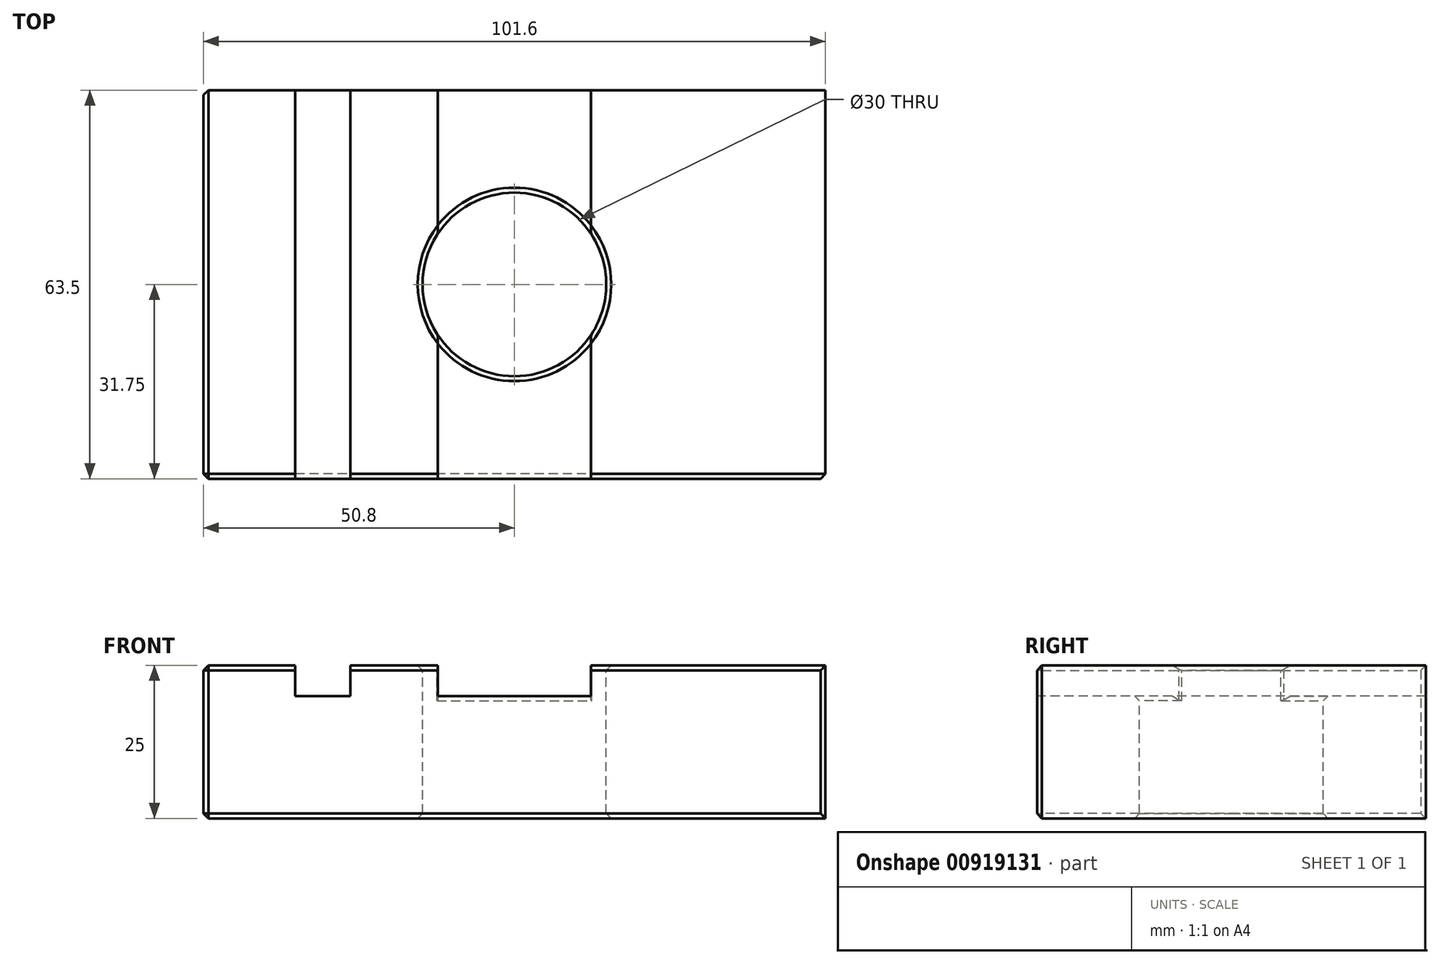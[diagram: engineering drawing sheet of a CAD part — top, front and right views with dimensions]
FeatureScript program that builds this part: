
annotation { "Feature Type Name" : "Feature", "Feature Type Description" : "" }
export const myFeature = defineFeature(function(context is Context, id is Id, definition is map)
    precondition{}
    {
        {
            var Q0;
            Q0=qCreatedBy(makeId("Top.planeOp"),FACE);
            var sketch = newSketch(context, id + "F0", { "sketchPlane" : qUnion([Q0])});
            skLineSegment(sketch, "E0.bottom", {"start": v(-50.8, -31.75) * mm, "end": v(50.8, -31.75) * mm});
            skLineSegment(sketch, "E0.top", {"start": v(-50.8, 31.75) * mm, "end": v(50.8, 31.75) * mm});
            skLineSegment(sketch, "E0.left", {"start": v(-50.8, -31.75) * mm, "end": v(-50.8, 31.75) * mm});
            skLineSegment(sketch, "E0.right", {"start": v(50.8, -31.75) * mm, "end": v(50.8, 31.75) * mm});
            skPoint(sketch, "E0.middle", {"position": v(0, 0) * mm});
            skSolve(sketch);
        }
        {
            var Q0;
            Q0=makeQuery(id+"F0.imprint","IMPRINT",FACE,{"disambiguationData":[TD([[makeQuery(id+"F0.imprint","IMPRINT",EDGE,{"derivedFrom":sQuery(id+"F0.wireOp",EDGE,"E0.bottom")}),1.0]])]});
            extrude(context, id + "F1", {"entities" : qUnion([Q0]), "depth" : 25 * mm, "offsetDistance" : 25.4 * mm});
        }
        {
            var Q0;
            Q0=makeQuery(id+"F1.opExtrude","CAP_FACE",FACE,{"disambiguationData":[OSD([sQuery(id+"F0.wireOp",EDGE,"E0.bottom"),sQuery(id+"F0.wireOp",EDGE,"E0.top"),sQuery(id+"F0.wireOp",EDGE,"E0.left"),sQuery(id+"F0.wireOp",EDGE,"E0.right")])],"isStart":false});
            var sketch = newSketch(context, id + "F2", { "sketchPlane" : qUnion([Q0])});
            skCircle(sketch, "E1", {"center": v(0, 0) * mm, "radius": 15 * mm});
            skSolve(sketch);
        }
        {
            var Q0;
            Q0=makeQuery(id+"F2.imprint","IMPRINT",FACE,{"disambiguationData":[TD([[makeQuery(id+"F2.imprint","IMPRINT",EDGE,{"derivedFrom":sQuery(id+"F2.wireOp",EDGE,"E1")}),1.0]])]});
            extrude(context, id + "F3", {"entities" : qUnion([Q0]), "operationType" : NewBodyOperationType.REMOVE, "endBound" : BoundingType.THROUGH_ALL, "oppositeDirection" : true, "depth" : 25 * mm, "offsetDistance" : 25 * mm});
        }
        {
            var Q0;
            Q0=makeQuery(id+"F1.opExtrude","CAP_FACE",FACE,{"disambiguationData":[OSD([sQuery(id+"F0.wireOp",EDGE,"E0.bottom"),sQuery(id+"F0.wireOp",EDGE,"E0.top"),sQuery(id+"F0.wireOp",EDGE,"E0.left"),sQuery(id+"F0.wireOp",EDGE,"E0.right")])],"isStart":false});
            var sketch = newSketch(context, id + "F4", { "sketchPlane" : qUnion([Q0])});
            skLineSegment(sketch, "E2", {"start": v(-35.8, 31.75) * mm, "end": v(-35.8, -31.75) * mm});
            skLineSegment(sketch, "E3", {"start": v(-35.8, -31.75) * mm, "end": v(-26.8, -31.75) * mm});
            skLineSegment(sketch, "E4", {"start": v(-26.8, -31.75) * mm, "end": v(-26.8, 31.75) * mm});
            skLineSegment(sketch, "E5", {"start": v(-26.8, 31.75) * mm, "end": v(-35.8, 31.75) * mm});
            skLineSegment(sketch, "E6", {"start": v(-12.5, 31.75) * mm, "end": v(-12.5, -31.75) * mm});
            skLineSegment(sketch, "E7", {"start": v(-12.5, -31.75) * mm, "end": v(12.5, -31.75) * mm});
            skLineSegment(sketch, "E8", {"start": v(12.5, -31.75) * mm, "end": v(12.5, 31.75) * mm});
            skLineSegment(sketch, "E9", {"start": v(12.5, 31.75) * mm, "end": v(-12.5, 31.75) * mm});
            skLineSegment(sketch, "E10", {"start": v(0, 31.75) * mm, "end": v(0, -31.75) * mm, "construction": true});
            skSolve(sketch);
        }
        {
            var Q0;
            {var subQ0=sQuery(id+"F4.wireOp",EDGE,"E9");Q0=makeQuery(id+"F4.imprint","IMPRINT",FACE,{"disambiguationData":[TD([[makeQuery(id+"F4.imprint","IMPRINT",EDGE,{"derivedFrom":subQ0}),-1.0]])]});}
            var Q1;
            Q1=makeQuery(id+"F4.imprint","IMPRINT",FACE,{"disambiguationData":[TD([[makeQuery(id+"F4.imprint","IMPRINT",EDGE,{"derivedFrom":sQuery(id+"F4.wireOp",EDGE,"E2")}),1.0]])]});
            var Q2;
            {var subQ0=sQuery(id+"F4.wireOp",EDGE,"E7");Q2=makeQuery(id+"F4.imprint","IMPRINT",FACE,{"disambiguationData":[TD([[makeQuery(id+"F4.imprint","IMPRINT",EDGE,{"derivedFrom":subQ0}),1.0]])]});}
            extrude(context, id + "F5", {"entities" : qUnion([Q0, Q1, Q2]), "operationType" : NewBodyOperationType.REMOVE, "oppositeDirection" : true, "depth" : 5 * mm, "offsetDistance" : 25 * mm});
        }
        {
            var Q0;
            {var subQ0=sQuery(id+"F2.wireOp",EDGE,"E1");var subQ1=makeQuery(id+"F3.boolean.opBoolean","COPY",EDGE,{"derivedFrom":makeQuery(id+"F3.opExtrude","CAP_EDGE",EDGE,{"disambiguationData":[OSD([subQ0])],"isStart":true})});Q0=makeQuery(id+"F5.boolean.opBoolean","COPY",EDGE,{"derivedFrom":makeQuery(id+"F5.opExtrude","CAP_EDGE",EDGE,{"disambiguationData":[OSD([subQ0]),TDD([makeQuery(id+"F4.imprint","IMPRINT",EDGE,{"disambiguationData":[TD([[makeQuery(id+"F4.imprint","INTERSECT",VERTEX,{"disambiguationData":[OD(1.0)],"derivedFrom":[subQ1,sQuery(id+"F4.wireOp",EDGE,"E6")]}),-1.0]])],"derivedFrom":subQ1})])],"isStart":false})});}
            var Q1;
            {var subQ0=sQuery(id+"F4.wireOp",EDGE,"E6");var subQ1=sQuery(id+"F2.wireOp",EDGE,"E1");Q1=makeQuery(id+"F5.boolean.opBoolean","COPY",EDGE,{"derivedFrom":makeQuery(id+"F5.opExtrude","SWEPT_EDGE",EDGE,{"disambiguationData":[OSD([subQ1,subQ0]),TDD([makeQuery(id+"F4.imprint","INTERSECT",VERTEX,{"disambiguationData":[OD(1.0)],"derivedFrom":[makeQuery(id+"F3.boolean.opBoolean","COPY",EDGE,{"derivedFrom":makeQuery(id+"F3.opExtrude","CAP_EDGE",EDGE,{"disambiguationData":[OSD([subQ1])],"isStart":true})}),subQ0]})])]})});}
            var Q2;
            {var subQ2=sQuery(id+"F2.wireOp",EDGE,"E1");var subQ3=sQuery(id+"F4.wireOp",EDGE,"E6");var subQ4=makeQuery(id+"F3.boolean.opBoolean","COPY",EDGE,{"derivedFrom":makeQuery(id+"F3.opExtrude","CAP_EDGE",EDGE,{"disambiguationData":[OSD([subQ2])],"isStart":true})});Q2=makeQuery(id+"F5.boolean.opBoolean","SPLIT",EDGE,{"disambiguationData":[TD([makeQuery(id+"F5.opExtrude","SWEPT_FACE",FACE,{"disambiguationData":[OSD([subQ3]),TDD([makeQuery(id+"F4.imprint","IMPRINT",EDGE,{"disambiguationData":[TD([[makeQuery(id+"F4.imprint","INTERSECT",VERTEX,{"disambiguationData":[OD(0.0)],"derivedFrom":[subQ4,subQ3]}),1.0]])],"derivedFrom":subQ3})])]})])],"derivedFrom":subQ4});}
            var Q3;
            {var subQ0=sQuery(id+"F4.wireOp",EDGE,"E6");var subQ1=sQuery(id+"F2.wireOp",EDGE,"E1");Q3=makeQuery(id+"F5.boolean.opBoolean","COPY",EDGE,{"derivedFrom":makeQuery(id+"F5.opExtrude","SWEPT_EDGE",EDGE,{"disambiguationData":[OSD([subQ1,subQ0]),TDD([makeQuery(id+"F4.imprint","INTERSECT",VERTEX,{"disambiguationData":[OD(0.0)],"derivedFrom":[makeQuery(id+"F3.boolean.opBoolean","COPY",EDGE,{"derivedFrom":makeQuery(id+"F3.opExtrude","CAP_EDGE",EDGE,{"disambiguationData":[OSD([subQ1])],"isStart":true})}),subQ0]})])]})});}
            var Q4;
            {var subQ0=sQuery(id+"F2.wireOp",EDGE,"E1");var subQ1=makeQuery(id+"F3.boolean.opBoolean","COPY",EDGE,{"derivedFrom":makeQuery(id+"F3.opExtrude","CAP_EDGE",EDGE,{"disambiguationData":[OSD([subQ0])],"isStart":true})});Q4=makeQuery(id+"F5.boolean.opBoolean","COPY",EDGE,{"derivedFrom":makeQuery(id+"F5.opExtrude","CAP_EDGE",EDGE,{"disambiguationData":[OSD([subQ0]),TDD([makeQuery(id+"F4.imprint","IMPRINT",EDGE,{"disambiguationData":[TD([[makeQuery(id+"F4.imprint","INTERSECT",VERTEX,{"disambiguationData":[OD(0.0)],"derivedFrom":[subQ1,sQuery(id+"F4.wireOp",EDGE,"E6")]}),1.0]])],"derivedFrom":subQ1})])],"isStart":false})});}
            var Q5;
            {var subQ2=sQuery(id+"F2.wireOp",EDGE,"E1");var subQ3=sQuery(id+"F4.wireOp",EDGE,"E8");var subQ4=makeQuery(id+"F3.boolean.opBoolean","COPY",EDGE,{"derivedFrom":makeQuery(id+"F3.opExtrude","CAP_EDGE",EDGE,{"disambiguationData":[OSD([subQ2])],"isStart":true})});Q5=makeQuery(id+"F5.boolean.opBoolean","SPLIT",EDGE,{"disambiguationData":[TD([makeQuery(id+"F5.opExtrude","SWEPT_FACE",FACE,{"disambiguationData":[OSD([subQ3]),TDD([makeQuery(id+"F4.imprint","IMPRINT",EDGE,{"disambiguationData":[TD([[makeQuery(id+"F4.imprint","INTERSECT",VERTEX,{"disambiguationData":[OD(0.0)],"derivedFrom":[subQ4,subQ3]}),1.0]])],"derivedFrom":subQ3})])]})])],"derivedFrom":subQ4});}
            var Q6;
            {var subQ0=sQuery(id+"F4.wireOp",EDGE,"E8");var subQ1=sQuery(id+"F2.wireOp",EDGE,"E1");Q6=makeQuery(id+"F5.boolean.opBoolean","COPY",EDGE,{"derivedFrom":makeQuery(id+"F5.opExtrude","SWEPT_EDGE",EDGE,{"disambiguationData":[OSD([subQ1,subQ0]),TDD([makeQuery(id+"F4.imprint","INTERSECT",VERTEX,{"disambiguationData":[OD(0.0)],"derivedFrom":[makeQuery(id+"F3.boolean.opBoolean","COPY",EDGE,{"derivedFrom":makeQuery(id+"F3.opExtrude","CAP_EDGE",EDGE,{"disambiguationData":[OSD([subQ1])],"isStart":true})}),subQ0]})])]})});}
            var Q7;
            {var subQ0=sQuery(id+"F4.wireOp",EDGE,"E8");var subQ1=sQuery(id+"F2.wireOp",EDGE,"E1");Q7=makeQuery(id+"F5.boolean.opBoolean","COPY",EDGE,{"derivedFrom":makeQuery(id+"F5.opExtrude","SWEPT_EDGE",EDGE,{"disambiguationData":[OSD([subQ1,subQ0]),TDD([makeQuery(id+"F4.imprint","INTERSECT",VERTEX,{"disambiguationData":[OD(1.0)],"derivedFrom":[makeQuery(id+"F3.boolean.opBoolean","COPY",EDGE,{"derivedFrom":makeQuery(id+"F3.opExtrude","CAP_EDGE",EDGE,{"disambiguationData":[OSD([subQ1])],"isStart":true})}),subQ0]})])]})});}
            var Q8;
            Q8=makeQuery(id+"F3.boolean.opBoolean","COPY",FACE,{"derivedFrom":makeQuery(id+"F3.opExtrude","SWEPT_FACE",FACE,{"disambiguationData":[OSD([sQuery(id+"F2.wireOp",EDGE,"E1")])]})});
            chamfer(context, id + "F6", {"entities" : qUnion([Q0, Q1, Q2, Q3, Q4, Q5, Q6, Q7, Q8]), "width" : .8 * mm, "tangentPropagation" : true});
        }
        {
            var Q0;
            {var subQ0=sQuery(id+"F0.wireOp",EDGE,"E0.bottom");var subQ2=makeQuery(id+"F1.opExtrude","CAP_EDGE",EDGE,{"disambiguationData":[OSD([subQ0])],"isStart":false});Q0=makeQuery(id+"F5.boolean.opBoolean","SPLIT",EDGE,{"disambiguationData":[TD([makeQuery(id+"F5.opExtrude","SWEPT_FACE",FACE,{"disambiguationData":[OSD([sQuery(id+"F4.wireOp",EDGE,"E4")])]})])],"derivedFrom":subQ2});}
            var Q1;
            {var subQ0=sQuery(id+"F0.wireOp",EDGE,"E0.bottom");var subQ1=sQuery(id+"F0.wireOp",EDGE,"E0.right");var subQ3=makeQuery(id+"F1.opExtrude","CAP_EDGE",EDGE,{"disambiguationData":[OSD([subQ0])],"isStart":false});Q1=makeQuery(id+"F5.boolean.opBoolean","SPLIT",EDGE,{"disambiguationData":[TD([makeQuery(id+"F1.opExtrude","SWEPT_FACE",FACE,{"disambiguationData":[OSD([subQ1])]})])],"derivedFrom":subQ3});}
            var Q2;
            {var subQ0=sQuery(id+"F0.wireOp",EDGE,"E0.bottom");var subQ1=sQuery(id+"F0.wireOp",EDGE,"E0.left");Q2=makeQuery(id+"F5.boolean.opBoolean","SPLIT",EDGE,{"disambiguationData":[TD([makeQuery(id+"F1.opExtrude","SWEPT_FACE",FACE,{"disambiguationData":[OSD([subQ1])]})])],"derivedFrom":makeQuery(id+"F1.opExtrude","CAP_EDGE",EDGE,{"disambiguationData":[OSD([subQ0])],"isStart":false})});}
            var Q3;
            Q3=makeQuery(id+"F5.boolean.opBoolean","COPY",EDGE,{"derivedFrom":makeQuery(id+"F5.opExtrude","SWEPT_EDGE",EDGE,{"disambiguationData":[OSD([sQuery(id+"F0.wireOp",EDGE,"E0.bottom"),sQuery(id+"F4.wireOp",EDGE,"E7"),sQuery(id+"F4.wireOp",EDGE,"E8")])]})});
            var Q4;
            Q4=makeQuery(id+"F5.boolean.opBoolean","COPY",EDGE,{"derivedFrom":makeQuery(id+"F5.opExtrude","CAP_EDGE",EDGE,{"disambiguationData":[OSD([sQuery(id+"F4.wireOp",EDGE,"E7")])],"isStart":false})});
            var Q5;
            Q5=makeQuery(id+"F5.boolean.opBoolean","COPY",EDGE,{"derivedFrom":makeQuery(id+"F5.opExtrude","SWEPT_EDGE",EDGE,{"disambiguationData":[OSD([sQuery(id+"F0.wireOp",EDGE,"E0.bottom"),sQuery(id+"F4.wireOp",EDGE,"E6"),sQuery(id+"F4.wireOp",EDGE,"E7")])]})});
            var Q6;
            Q6=makeQuery(id+"F5.boolean.opBoolean","COPY",EDGE,{"derivedFrom":makeQuery(id+"F5.opExtrude","SWEPT_EDGE",EDGE,{"disambiguationData":[OSD([sQuery(id+"F0.wireOp",EDGE,"E0.bottom"),sQuery(id+"F4.wireOp",EDGE,"E3"),sQuery(id+"F4.wireOp",EDGE,"E4")])]})});
            var Q7;
            Q7=makeQuery(id+"F5.boolean.opBoolean","COPY",EDGE,{"derivedFrom":makeQuery(id+"F5.opExtrude","CAP_EDGE",EDGE,{"disambiguationData":[OSD([sQuery(id+"F4.wireOp",EDGE,"E3")])],"isStart":false})});
            var Q8;
            Q8=makeQuery(id+"F5.boolean.opBoolean","COPY",EDGE,{"derivedFrom":makeQuery(id+"F5.opExtrude","SWEPT_EDGE",EDGE,{"disambiguationData":[OSD([sQuery(id+"F0.wireOp",EDGE,"E0.bottom"),sQuery(id+"F4.wireOp",EDGE,"E2"),sQuery(id+"F4.wireOp",EDGE,"E3")])]})});
            var Q9;
            Q9=makeQuery(id+"F1.opExtrude","SWEPT_EDGE",EDGE,{"disambiguationData":[OSD([sQuery(id+"F0.wireOp",EDGE,"E0.bottom"),sQuery(id+"F0.wireOp",EDGE,"E0.left")])]});
            var Q10;
            Q10=makeQuery(id+"F1.opExtrude","CAP_EDGE",EDGE,{"disambiguationData":[OSD([sQuery(id+"F0.wireOp",EDGE,"E0.bottom")])],"isStart":true});
            var Q11;
            Q11=makeQuery(id+"F1.opExtrude","SWEPT_EDGE",EDGE,{"disambiguationData":[OSD([sQuery(id+"F0.wireOp",EDGE,"E0.bottom"),sQuery(id+"F0.wireOp",EDGE,"E0.right")])]});
            var Q12;
            Q12=makeQuery(id+"F1.opExtrude","CAP_EDGE",EDGE,{"disambiguationData":[OSD([sQuery(id+"F0.wireOp",EDGE,"E0.left")])],"isStart":false});
            var Q13;
            Q13=makeQuery(id+"F1.opExtrude","CAP_EDGE",EDGE,{"disambiguationData":[OSD([sQuery(id+"F0.wireOp",EDGE,"E0.left")])],"isStart":true});
            var Q14;
            Q14=makeQuery(id+"F1.opExtrude","SWEPT_EDGE",EDGE,{"disambiguationData":[OSD([sQuery(id+"F0.wireOp",EDGE,"E0.top"),sQuery(id+"F0.wireOp",EDGE,"E0.left")])]});
            chamfer(context, id + "F7", {"entities" : qUnion([Q0, Q1, Q2, Q3, Q4, Q5, Q6, Q7, Q8, Q9, Q10, Q11, Q12, Q13, Q14]), "width" : .8 * mm, "tangentPropagation" : true});
        }
    });
